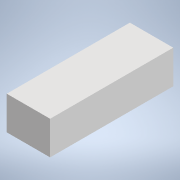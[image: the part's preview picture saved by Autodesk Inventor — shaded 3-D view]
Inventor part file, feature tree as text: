
AUTODESK INVENTOR PART (.ipt)
format: ipt  version: 2022 (Build 260153070, 153G)  size: 88,064 bytes
history: native  units: mm
features: extrude x1, sketch x1
ambient origin geometry x8: Origin, YZ Plane, XZ Plane, XY Plane, X Axis, Y Axis, Z Axis, Center Point
bodies: Solid1 (feature_tree)
feature tree (2):
  extrude  "Extrusion1"  Depth=14.25mm
  sketch  "Sketch1"  dims[d0=18.5mm d1=14.25mm d2=52.5mm d3=0.0mm]
